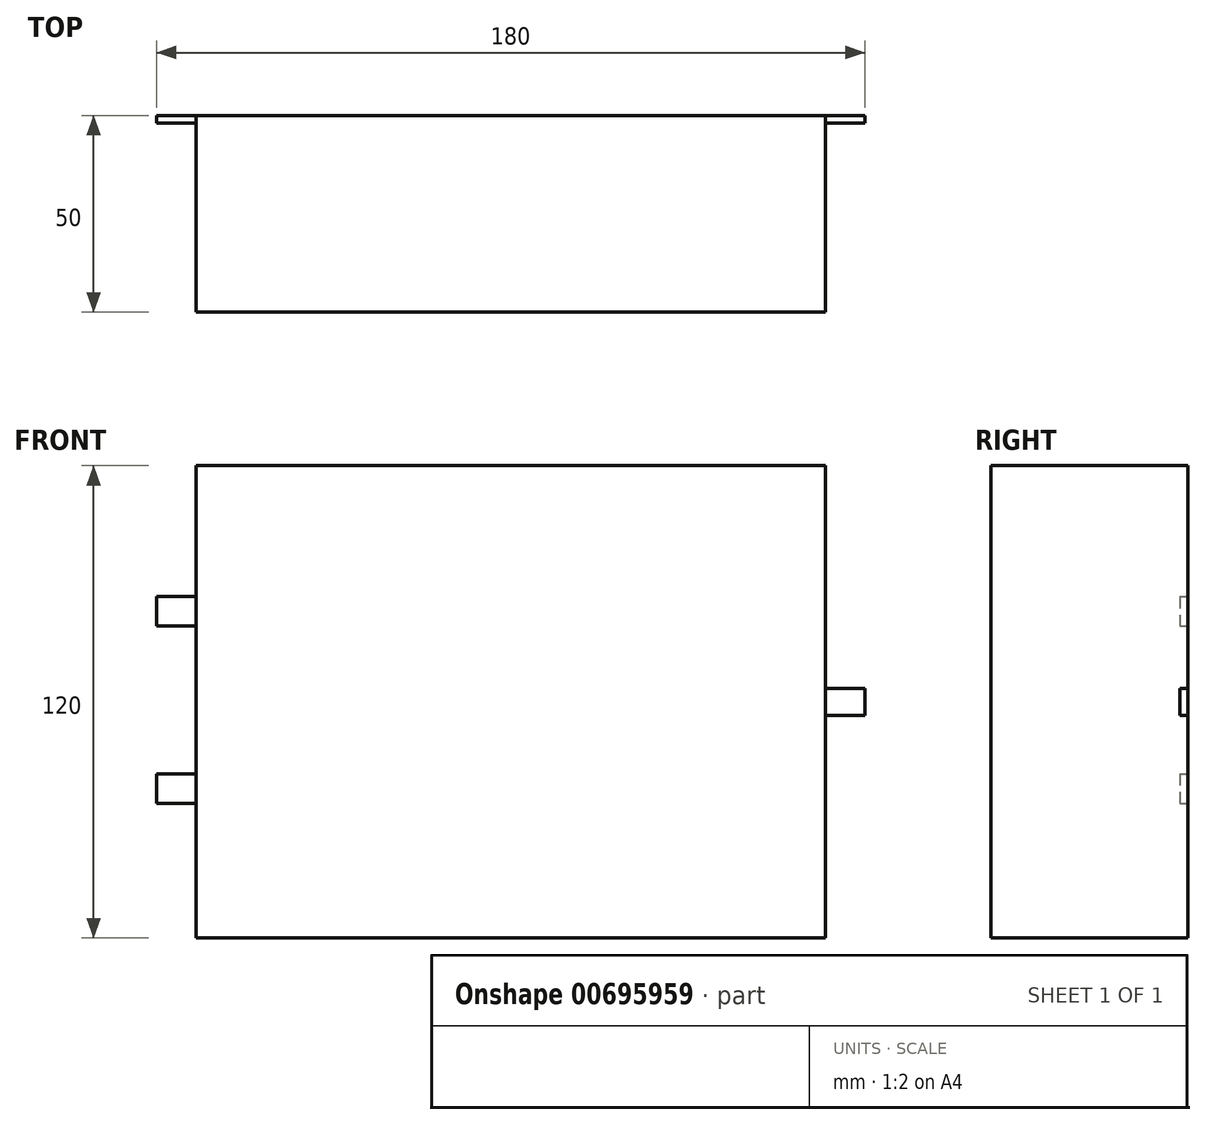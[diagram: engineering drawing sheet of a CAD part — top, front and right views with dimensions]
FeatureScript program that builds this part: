
annotation { "Feature Type Name" : "Feature", "Feature Type Description" : "" }
export const myFeature = defineFeature(function(context is Context, id is Id, definition is map)
    precondition{}
    {
        {
            var Q0;
            Q0=qCreatedBy(makeId("Front.planeOp"),FACE);
            var sketch = newSketch(context, id + "F0", { "sketchPlane" : qUnion([Q0])});
            skLineSegment(sketch, "E0.bottom", {"start": v(80, 60) * mm, "end": v(-80, 60) * mm});
            skLineSegment(sketch, "E0.top", {"start": v(80, -60) * mm, "end": v(-80, -60) * mm});
            skLineSegment(sketch, "E0.left", {"start": v(80, 60) * mm, "end": v(80, -60) * mm});
            skLineSegment(sketch, "E0.right", {"start": v(-80, 60) * mm, "end": v(-80, -60) * mm});
            skPoint(sketch, "E0.middle", {"position": v(0, 0) * mm});
            skLineSegment(sketch, "E1.bottom", {"start": v(-80, 26.75) * mm, "end": v(-90, 26.75) * mm});
            skLineSegment(sketch, "E1.top", {"start": v(-80, 19.25) * mm, "end": v(-90, 19.25) * mm});
            skLineSegment(sketch, "E1.left", {"start": v(-80, 26.75) * mm, "end": v(-80, 19.25) * mm});
            skLineSegment(sketch, "E1.right", {"start": v(-90, 26.75) * mm, "end": v(-90, 19.25) * mm});
            skPoint(sketch, "E1.middle", {"position": v(-85, 23) * mm});
            skLineSegment(sketch, "E2.bottom", {"start": v(-80, -18.25) * mm, "end": v(-90, -18.25) * mm});
            skLineSegment(sketch, "E2.top", {"start": v(-80, -25.75) * mm, "end": v(-90, -25.75) * mm});
            skLineSegment(sketch, "E2.left", {"start": v(-80, -18.25) * mm, "end": v(-80, -25.75) * mm});
            skLineSegment(sketch, "E2.right", {"start": v(-90, -18.25) * mm, "end": v(-90, -25.75) * mm});
            skPoint(sketch, "E2.middle", {"position": v(-85, -22) * mm});
            skLineSegment(sketch, "E3.bottom", {"start": v(80, -3.44) * mm, "end": v(90, -3.44) * mm});
            skLineSegment(sketch, "E3.top", {"start": v(80, 3.44) * mm, "end": v(90, 3.44) * mm});
            skLineSegment(sketch, "E3.left", {"start": v(80, -3.44) * mm, "end": v(80, 3.44) * mm});
            skLineSegment(sketch, "E3.right", {"start": v(90, -3.44) * mm, "end": v(90, 3.44) * mm});
            skPoint(sketch, "E3.middle", {"position": v(85, 0) * mm});
            skSolve(sketch);
        }
        {
            var Q0;
            {var subQ3=sQuery(id+"F0.wireOp",EDGE,"E0.bottom");Q0=makeQuery(id+"F0.imprint","IMPRINT",FACE,{"disambiguationData":[TD([[makeQuery(id+"F0.imprint","IMPRINT",EDGE,{"derivedFrom":subQ3}),1.0]])]});}
            extrude(context, id + "F1", {"entities" : qUnion([Q0]), "depth" : 50 * mm, "offsetDistance" : 25 * mm});
        }
        {
            var Q0;
            Q0=makeQuery(id+"F0.imprint","IMPRINT",FACE,{"disambiguationData":[TD([[makeQuery(id+"F0.imprint","IMPRINT",EDGE,{"derivedFrom":sQuery(id+"F0.wireOp",EDGE,"E2.bottom")}),1.0]])]});
            var Q1;
            Q1=makeQuery(id+"F0.imprint","IMPRINT",FACE,{"disambiguationData":[TD([[makeQuery(id+"F0.imprint","IMPRINT",EDGE,{"derivedFrom":sQuery(id+"F0.wireOp",EDGE,"E1.bottom")}),1.0]])]});
            var Q2;
            Q2=makeQuery(id+"F0.imprint","IMPRINT",FACE,{"disambiguationData":[TD([[makeQuery(id+"F0.imprint","IMPRINT",EDGE,{"derivedFrom":sQuery(id+"F0.wireOp",EDGE,"E3.bottom")}),1.0]])]});
            extrude(context, id + "F2", {"entities" : qUnion([Q0, Q1, Q2]), "operationType" : NewBodyOperationType.ADD, "depth" : 2 * mm, "offsetDistance" : 25 * mm});
        }
    });
